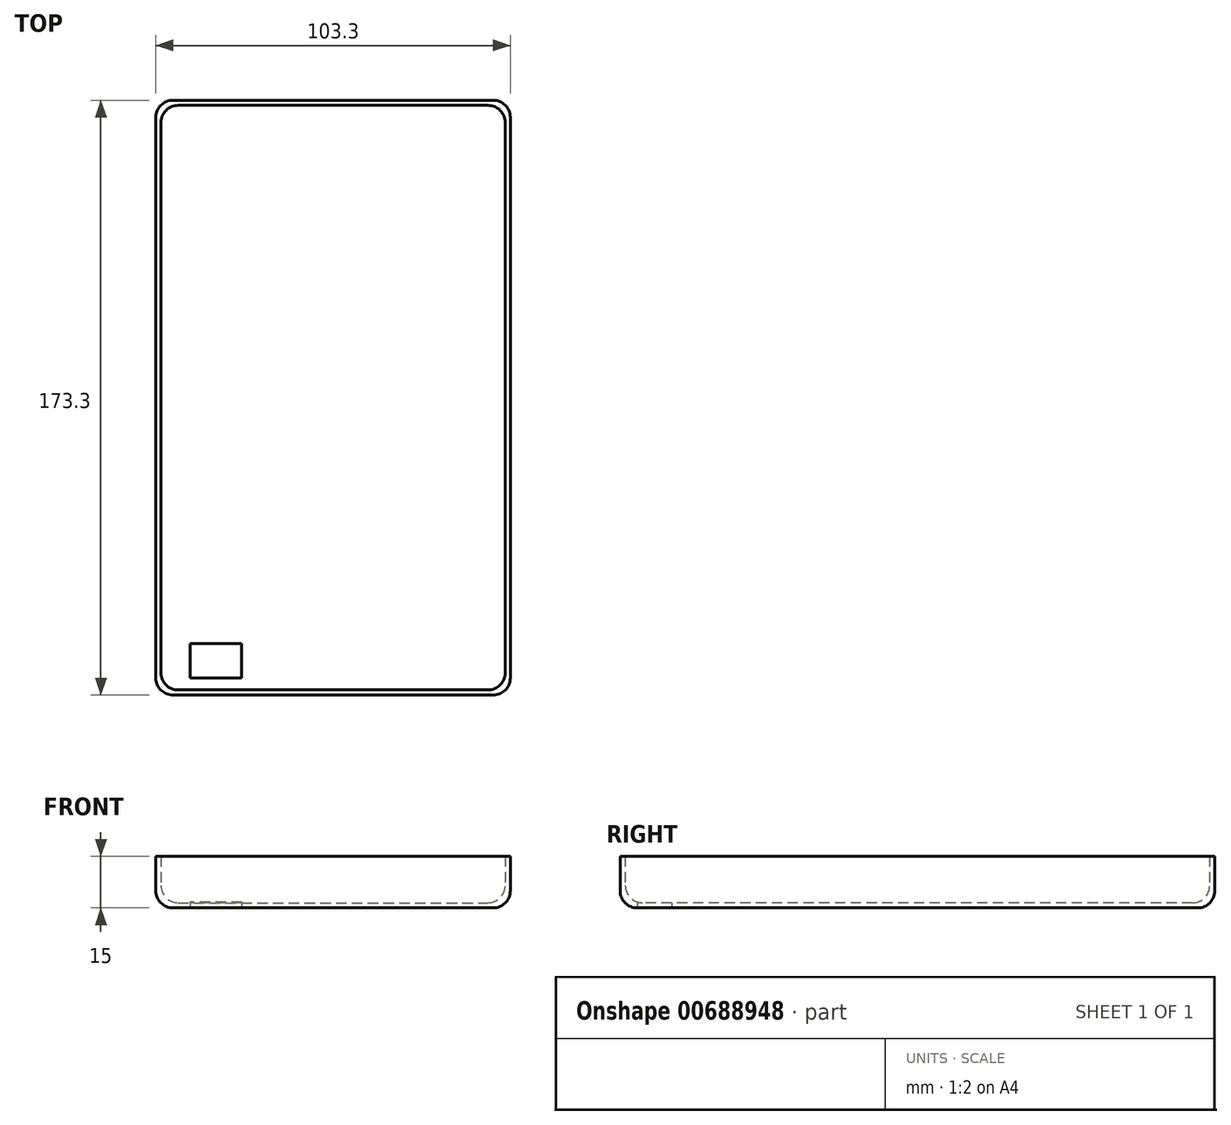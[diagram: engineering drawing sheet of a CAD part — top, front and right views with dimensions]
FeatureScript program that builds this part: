
annotation { "Feature Type Name" : "Feature", "Feature Type Description" : "" }
export const myFeature = defineFeature(function(context is Context, id is Id, definition is map)
    precondition{}
    {
        {
            var Q0;
            Q0=qCreatedBy(makeId("Top.planeOp"),FACE);
            var sketch = newSketch(context, id + "F0", { "sketchPlane" : qUnion([Q0])});
            skLineSegment(sketch, "E0.bottom", {"start": v(0, 0) * mm, "end": v(100.3, 0) * mm});
            skLineSegment(sketch, "E0.top", {"start": v(0, -170.3) * mm, "end": v(100.3, -170.3) * mm});
            skLineSegment(sketch, "E0.left", {"start": v(0, 0) * mm, "end": v(0, -170.3) * mm});
            skLineSegment(sketch, "E0.right", {"start": v(100.3, 0) * mm, "end": v(100.3, -170.3) * mm});
            skLineSegment(sketch, "E1.bottom", {"start": v(-1.5, 1.5) * mm, "end": v(101.8, 1.5) * mm});
            skLineSegment(sketch, "E1.top", {"start": v(-1.5, -171.8) * mm, "end": v(101.8, -171.8) * mm});
            skLineSegment(sketch, "E1.left", {"start": v(-1.5, 1.5) * mm, "end": v(-1.5, -171.8) * mm});
            skLineSegment(sketch, "E1.right", {"start": v(101.8, 1.5) * mm, "end": v(101.8, -171.8) * mm});
            skLineSegment(sketch, "E2", {"start": v(0, 0) * mm, "end": v(0, 1.5) * mm, "construction": true});
            skLineSegment(sketch, "E3", {"start": v(0, 0) * mm, "end": v(-1.5, 0) * mm, "construction": true});
            skSolve(sketch);
        }
        {
            var Q0;
            Q0=makeQuery(id+"F0.imprint","IMPRINT",FACE,{"disambiguationData":[TD([[makeQuery(id+"F0.imprint","IMPRINT",EDGE,{"derivedFrom":sQuery(id+"F0.wireOp",EDGE,"E0.bottom")}),-1.0]])]});
            extrude(context, id + "F1", {"entities" : qUnion([Q0]), "depth" : 1.5 * mm, "offsetDistance" : 25 * mm});
        }
        {
            var Q0;
            Q0=makeQuery(id+"F0.imprint","IMPRINT",FACE,{"disambiguationData":[TD([[makeQuery(id+"F0.imprint","IMPRINT",EDGE,{"derivedFrom":sQuery(id+"F0.wireOp",EDGE,"E0.bottom")}),1.0]])]});
            extrude(context, id + "F2", {"entities" : qUnion([Q0]), "operationType" : NewBodyOperationType.ADD, "depth" : 15 * mm, "offsetDistance" : 25 * mm});
        }
        {
            var Q0;
            Q0=makeQuery(id+"F2.opExtrude","SWEPT_EDGE",EDGE,{"disambiguationData":[OSD([sQuery(id+"F0.wireOp",EDGE,"E0.bottom"),sQuery(id+"F0.wireOp",EDGE,"E0.left")])]});
            var Q1;
            Q1=makeQuery(id+"F2.opExtrude","SWEPT_EDGE",EDGE,{"disambiguationData":[OSD([sQuery(id+"F0.wireOp",EDGE,"E1.bottom"),sQuery(id+"F0.wireOp",EDGE,"E1.right")])]});
            var Q2;
            Q2=makeQuery(id+"F2.opExtrude","SWEPT_EDGE",EDGE,{"disambiguationData":[OSD([sQuery(id+"F0.wireOp",EDGE,"E0.bottom"),sQuery(id+"F0.wireOp",EDGE,"E0.right")])]});
            var Q3;
            Q3=makeQuery(id+"F2.opExtrude","SWEPT_EDGE",EDGE,{"disambiguationData":[OSD([sQuery(id+"F0.wireOp",EDGE,"E1.bottom"),sQuery(id+"F0.wireOp",EDGE,"E1.left")])]});
            var Q4;
            Q4=makeQuery(id+"F2.opExtrude","SWEPT_EDGE",EDGE,{"disambiguationData":[OSD([sQuery(id+"F0.wireOp",EDGE,"E0.top"),sQuery(id+"F0.wireOp",EDGE,"E0.right")])]});
            var Q5;
            Q5=makeQuery(id+"F2.opExtrude","SWEPT_EDGE",EDGE,{"disambiguationData":[OSD([sQuery(id+"F0.wireOp",EDGE,"E1.top"),sQuery(id+"F0.wireOp",EDGE,"E1.left")])]});
            var Q6;
            Q6=makeQuery(id+"F2.opExtrude","SWEPT_EDGE",EDGE,{"disambiguationData":[OSD([sQuery(id+"F0.wireOp",EDGE,"E0.top"),sQuery(id+"F0.wireOp",EDGE,"E0.left")])]});
            var Q7;
            Q7=makeQuery(id+"F2.opExtrude","SWEPT_EDGE",EDGE,{"disambiguationData":[OSD([sQuery(id+"F0.wireOp",EDGE,"E1.top"),sQuery(id+"F0.wireOp",EDGE,"E1.right")])]});
            var Q8;
            {var subQ0=sQuery(id+"F0.wireOp",EDGE,"E0.right");var subQ1=sQuery(id+"F0.wireOp",EDGE,"E0.left");var subQ2=sQuery(id+"F0.wireOp",EDGE,"E0.top");var subQ3=sQuery(id+"F0.wireOp",EDGE,"E0.bottom");Q8=makeQuery(id+"F2.boolean.opBoolean","MERGE",FACE,{"derivedFrom":[makeQuery(id+"F1.opExtrude","CAP_FACE",FACE,{"disambiguationData":[OSD([subQ3,subQ2,subQ1,subQ0])],"isStart":true}),makeQuery(id+"F2.opExtrude","CAP_FACE",FACE,{"disambiguationData":[OSD([subQ3,subQ2,subQ1,subQ0,sQuery(id+"F0.wireOp",EDGE,"E1.bottom"),sQuery(id+"F0.wireOp",EDGE,"E1.top"),sQuery(id+"F0.wireOp",EDGE,"E1.left"),sQuery(id+"F0.wireOp",EDGE,"E1.right")])],"isStart":true})]});}
            var Q9;
            Q9=makeQuery(id+"F1.opExtrude","CAP_FACE",FACE,{"disambiguationData":[OSD([sQuery(id+"F0.wireOp",EDGE,"E0.bottom"),sQuery(id+"F0.wireOp",EDGE,"E0.top"),sQuery(id+"F0.wireOp",EDGE,"E0.left"),sQuery(id+"F0.wireOp",EDGE,"E0.right")])],"isStart":false});
            fillet(context, id + "F3", {"entities" : qUnion([Q0, Q1, Q2, Q3, Q4, Q5, Q6, Q7, Q8, Q9]), "radius" : 5 * mm, "tangentPropagation" : true, "allowEdgeOverflow" : false});
        }
        {
            var Q0;
            {var subQ0=sQuery(id+"F0.wireOp",EDGE,"E0.right");var subQ1=sQuery(id+"F0.wireOp",EDGE,"E0.left");var subQ2=sQuery(id+"F0.wireOp",EDGE,"E0.top");var subQ3=sQuery(id+"F0.wireOp",EDGE,"E0.bottom");Q0=makeQuery(id+"F2.boolean.opBoolean","MERGE",FACE,{"derivedFrom":[makeQuery(id+"F1.opExtrude","CAP_FACE",FACE,{"disambiguationData":[OSD([subQ3,subQ2,subQ1,subQ0])],"isStart":true}),makeQuery(id+"F2.opExtrude","CAP_FACE",FACE,{"disambiguationData":[OSD([subQ3,subQ2,subQ1,subQ0,sQuery(id+"F0.wireOp",EDGE,"E1.bottom"),sQuery(id+"F0.wireOp",EDGE,"E1.top"),sQuery(id+"F0.wireOp",EDGE,"E1.left"),sQuery(id+"F0.wireOp",EDGE,"E1.right")])],"isStart":true})]});}
            var sketch = newSketch(context, id + "F4", { "sketchPlane" : qUnion([Q0])});
            skLineSegment(sketch, "E4.bottom", {"start": v(8.5, 166.8) * mm, "end": v(23.5, 166.8) * mm});
            skLineSegment(sketch, "E4.top", {"start": v(8.5, 156.8) * mm, "end": v(23.5, 156.8) * mm});
            skLineSegment(sketch, "E4.left", {"start": v(8.5, 166.8) * mm, "end": v(8.5, 156.8) * mm});
            skLineSegment(sketch, "E4.right", {"start": v(23.5, 166.8) * mm, "end": v(23.5, 156.8) * mm});
            skLineSegment(sketch, "E5", {"start": v(8.5, 166.8) * mm, "end": v(3.5, 166.8) * mm, "construction": true});
            skSolve(sketch);
        }
        {
            var Q0;
            Q0 = qSketchRegion(id + "F4", true);
            extrude(context, id + "F5", {"entities" : qUnion([Q0]), "operationType" : NewBodyOperationType.REMOVE, "oppositeDirection" : true, "depth" : 25 * mm, "offsetDistance" : 25 * mm});
        }
    });
